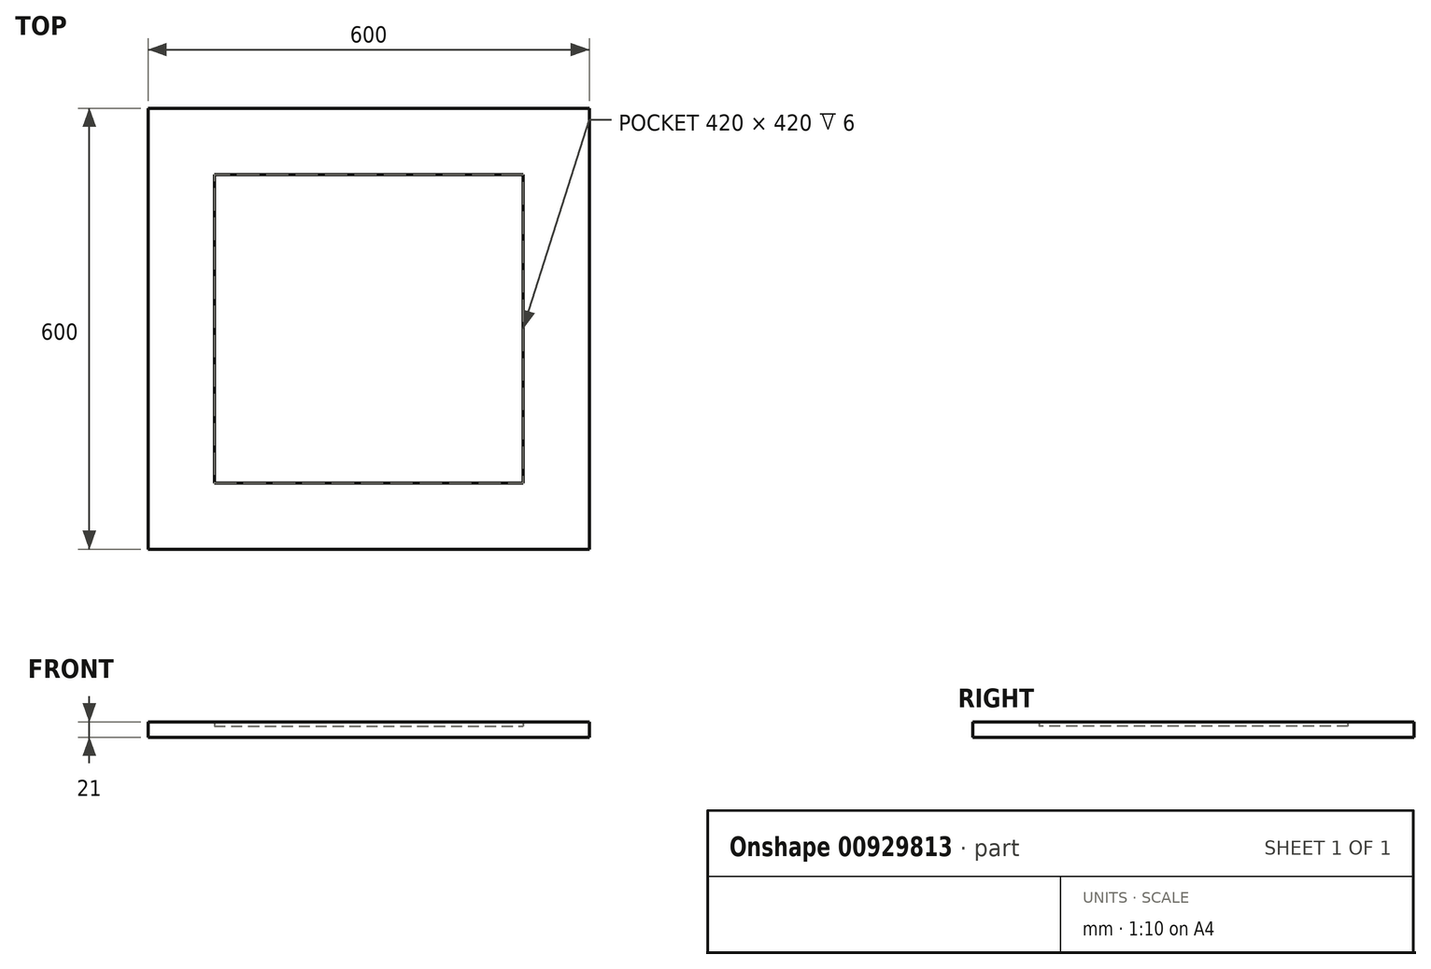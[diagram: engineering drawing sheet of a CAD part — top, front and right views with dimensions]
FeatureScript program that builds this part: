
annotation { "Feature Type Name" : "Feature", "Feature Type Description" : "" }
export const myFeature = defineFeature(function(context is Context, id is Id, definition is map)
    precondition{}
    {
        {
            var Q0;
            Q0=qCreatedBy(makeId("Top.planeOp"),FACE);
            var sketch = newSketch(context, id + "F0", { "sketchPlane" : qUnion([Q0])});
            skLineSegment(sketch, "E0.bottom", {"start": v(300, 300) * mm, "end": v(-300, 300) * mm});
            skLineSegment(sketch, "E0.top", {"start": v(300, -300) * mm, "end": v(-300, -300) * mm});
            skLineSegment(sketch, "E0.left", {"start": v(300, 300) * mm, "end": v(300, -300) * mm});
            skLineSegment(sketch, "E0.right", {"start": v(-300, 300) * mm, "end": v(-300, -300) * mm});
            skPoint(sketch, "E0.middle", {"position": v(0, 0) * mm});
            skSolve(sketch);
        }
        {
            var Q0;
            Q0=qSketchRegion(id+"F0",true);
            extrude(context, id + "F1", {"entities" : qUnion([Q0]), "depth" : 15 * mm, "offsetDistance" : 25 * mm});
        }
        {
            var Q0;
            Q0=makeQuery(id+"F1.opExtrude","CAP_FACE",FACE,{"disambiguationData":[OSD([sQuery(id+"F0.wireOp",EDGE,"E0.bottom"),sQuery(id+"F0.wireOp",EDGE,"E0.top"),sQuery(id+"F0.wireOp",EDGE,"E0.left"),sQuery(id+"F0.wireOp",EDGE,"E0.right")])],"isStart":false});
            var sketch = newSketch(context, id + "F2", { "sketchPlane" : qUnion([Q0])});
            skLineSegment(sketch, "E1", {"start": v(-300, 300) * mm, "end": v(-300, -300) * mm});
            skLineSegment(sketch, "E2", {"start": v(-300, -300) * mm, "end": v(-210, -210) * mm});
            skLineSegment(sketch, "E3", {"start": v(-210, -210) * mm, "end": v(-210, 210) * mm});
            skLineSegment(sketch, "E4", {"start": v(-210, 210) * mm, "end": v(-300, 300) * mm});
            skLineSegment(sketch, "E5", {"start": v(300, 300) * mm, "end": v(210, 210) * mm});
            skLineSegment(sketch, "E6", {"start": v(210, 210) * mm, "end": v(210, -210) * mm});
            skLineSegment(sketch, "E7", {"start": v(210, -210) * mm, "end": v(300, -300) * mm});
            skLineSegment(sketch, "E8", {"start": v(300, -300) * mm, "end": v(300, 300) * mm});
            skLineSegment(sketch, "E9", {"start": v(-210, 210) * mm, "end": v(210, 210) * mm});
            skLineSegment(sketch, "E10", {"start": v(210, 210) * mm, "end": v(300, 300) * mm});
            skLineSegment(sketch, "E11", {"start": v(300, 300) * mm, "end": v(-300, 300) * mm});
            skLineSegment(sketch, "E12", {"start": v(-300, 300) * mm, "end": v(-210, 210) * mm});
            skLineSegment(sketch, "E13", {"start": v(-210, -210) * mm, "end": v(210, -210) * mm});
            skLineSegment(sketch, "E14", {"start": v(300, -300) * mm, "end": v(-300, -300) * mm});
            skSolve(sketch);
        }
        {
            var Q0;
            Q0=makeQuery(id+"F2.imprint","IMPRINT",FACE,{"disambiguationData":[TD([[makeQuery(id+"F2.imprint","IMPRINT",EDGE,{"derivedFrom":sQuery(id+"F2.wireOp",EDGE,"E3")}),-1.0]])]});
            var sketch = newSketch(context, id + "F3", { "sketchPlane" : qUnion([Q0])});
            skLineSegment(sketch, "E15.bottom", {"start": v(325, 325) * mm, "end": v(-325, 325) * mm});
            skLineSegment(sketch, "E15.top", {"start": v(325, -325) * mm, "end": v(-325, -325) * mm});
            skLineSegment(sketch, "E15.left", {"start": v(325, 325) * mm, "end": v(325, -325) * mm});
            skLineSegment(sketch, "E15.right", {"start": v(-325, 325) * mm, "end": v(-325, -325) * mm});
            skPoint(sketch, "E15.middle", {"position": v(0, 0) * mm});
            skLineSegment(sketch, "E16.bottom", {"start": v(300, 300) * mm, "end": v(-300, 300) * mm});
            skLineSegment(sketch, "E16.top", {"start": v(300, -300) * mm, "end": v(-300, -300) * mm});
            skLineSegment(sketch, "E16.left", {"start": v(300, 300) * mm, "end": v(300, -300) * mm});
            skLineSegment(sketch, "E16.right", {"start": v(-300, 300) * mm, "end": v(-300, -300) * mm});
            skSolve(sketch);
        }
        {
            var Q0;
            Q0=makeQuery(id+"F3.imprint","IMPRINT",FACE,{"disambiguationData":[TD([[makeQuery(id+"F3.imprint","IMPRINT",EDGE,{"derivedFrom":sQuery(id+"F3.wireOp",EDGE,"E16.bottom")}),1.0]])]});
            extrude(context, id + "F4", {"entities" : qUnion([Q0]), "operationType" : NewBodyOperationType.ADD, "depth" : 6 * mm, "offsetDistance" : 25 * mm});
        }
    });
